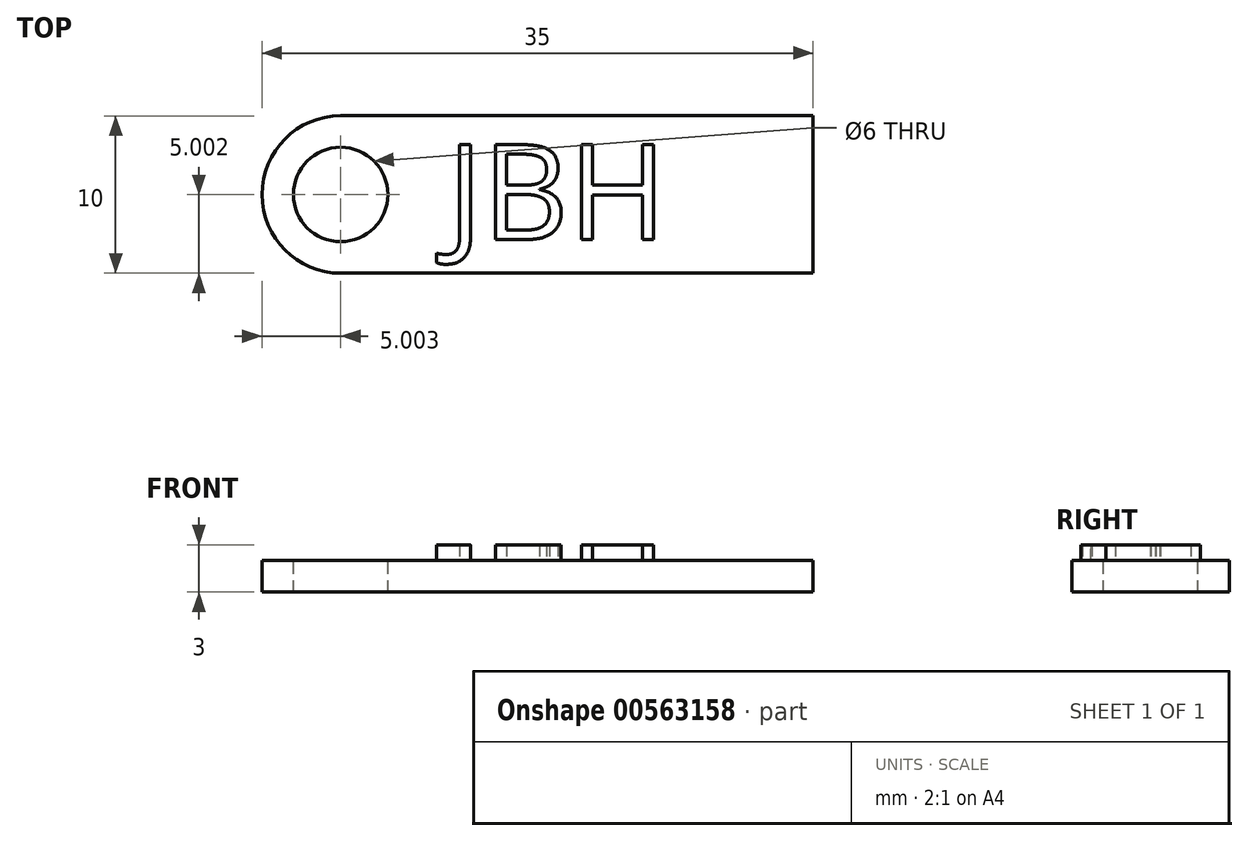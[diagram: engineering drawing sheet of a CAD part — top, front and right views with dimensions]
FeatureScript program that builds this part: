
annotation { "Feature Type Name" : "Feature", "Feature Type Description" : "" }
export const myFeature = defineFeature(function(context is Context, id is Id, definition is map)
    precondition{}
    {
        {
            var Q0;
            Q0=qCreatedBy(makeId("Top.planeOp"),FACE);
            var sketch = newSketch(context, id + "F0", { "sketchPlane" : qUnion([Q0])});
            skLineSegment(sketch, "E0.bottom", {"start": v(-45.14, 11.82) * mm, "end": v(-15.14, 11.82) * mm});
            skLineSegment(sketch, "E0.top", {"start": v(-45.14, 1.82) * mm, "end": v(-15.14, 1.82) * mm});
            skLineSegment(sketch, "E0.left", {"start": v(-45.14, 11.82) * mm, "end": v(-45.14, 1.82) * mm});
            skLineSegment(sketch, "E0.right", {"start": v(-15.14, 11.82) * mm, "end": v(-15.14, 1.82) * mm});
            skArc(sketch, "E1", {"start": v(-45.14, 1.82) * mm, "mid": v(-50.14, 6.82) * mm, "end": v(-45.14, 11.82) * mm});
            skSolve(sketch);
        }
        {
            var Q0;
            Q0 = qSketchRegion(id + "F0", true);
            extrude(context, id + "F1", {"entities" : qUnion([Q0]), "depth" : 2 * mm, "offsetDistance" : 25 * mm});
        }
        {
            var Q0;
            Q0=makeQuery(id+"F1.opExtrude","CAP_FACE",FACE,{"disambiguationData":[OSD([sQuery(id+"F0.wireOp",EDGE,"E0.bottom"),sQuery(id+"F0.wireOp",EDGE,"E0.top"),sQuery(id+"F0.wireOp",EDGE,"E0.right"),sQuery(id+"F0.wireOp",EDGE,"E1")])],"isStart":false});
            var sketch = newSketch(context, id + "F2", { "sketchPlane" : qUnion([Q0])});
            skCircle(sketch, "E2", {"center": v(-45.14, 6.82) * mm, "radius": 3 * mm});
            skSolve(sketch);
        }
        {
            var Q0;
            Q0 = qSketchRegion(id + "F2", true);
            extrude(context, id + "F3", {"entities" : qUnion([Q0]), "operationType" : NewBodyOperationType.REMOVE, "oppositeDirection" : true, "depth" : 5 * mm, "offsetDistance" : 25 * mm, "symmetric" : true});
        }
        {
            var Q0;
            Q0=makeQuery(id+"F1.opExtrude","CAP_FACE",FACE,{"disambiguationData":[OSD([sQuery(id+"F0.wireOp",EDGE,"E0.bottom"),sQuery(id+"F0.wireOp",EDGE,"E0.top"),sQuery(id+"F0.wireOp",EDGE,"E0.right"),sQuery(id+"F0.wireOp",EDGE,"E1")])],"isStart":false});
            var sketch = newSketch(context, id + "F4", { "sketchPlane" : qUnion([Q0])});
            skText(sketch, "E3", { "text": "JBH", "fontName": "OpenSans-Regular.ttf"});
            const initialGuessF4  = {"E3": [-0.03838, 0.00397, 1, 0, 0.00607]};
            skSetInitialGuess(sketch, initialGuessF4);
            skSolve(sketch);
        }
        {
            var Q0;
            Q0 = qSketchRegion(id + "F4", true);
            extrude(context, id + "F5", {"entities" : qUnion([Q0]), "operationType" : NewBodyOperationType.ADD, "depth" : 1 * mm, "offsetDistance" : 25 * mm});
        }
    });
